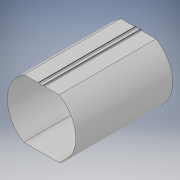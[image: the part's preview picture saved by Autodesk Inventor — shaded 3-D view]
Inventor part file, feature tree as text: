
AUTODESK INVENTOR PART (.ipt)
format: ipt  version: 2017 (Build 210142000, 142)  size: 135,680 bytes
history: native  units: in
note: dims shown in document units (in); Inventor stores cm internally (conversion verified against a paired STEP export)
features: other x1, delete_face x1, sketch x1
ambient origin geometry x8: Origin, YZ Plane, XZ Plane, XY Plane, X Axis, Y Axis, Z Axis, Center Point
bodies: Solid1 (feature_tree)
feature tree (3):
  other  "corridor"
  delete_face  "Delete Face1"
  sketch  "Sketch1"  dims[d0=6.6667in d1=4.0in d2=1.0in d3=11.0in d4=0.0in d7=1.0in d23=0.5833in d26=0.125in d27=3.8873in d28=3.8873in d30=1.7083in d39=0.0625in d40=0.0625in d41=1.6458in d51=0.25in d52=0.125in d54=0.0884in d55=45.0deg d56=3.3333in]
